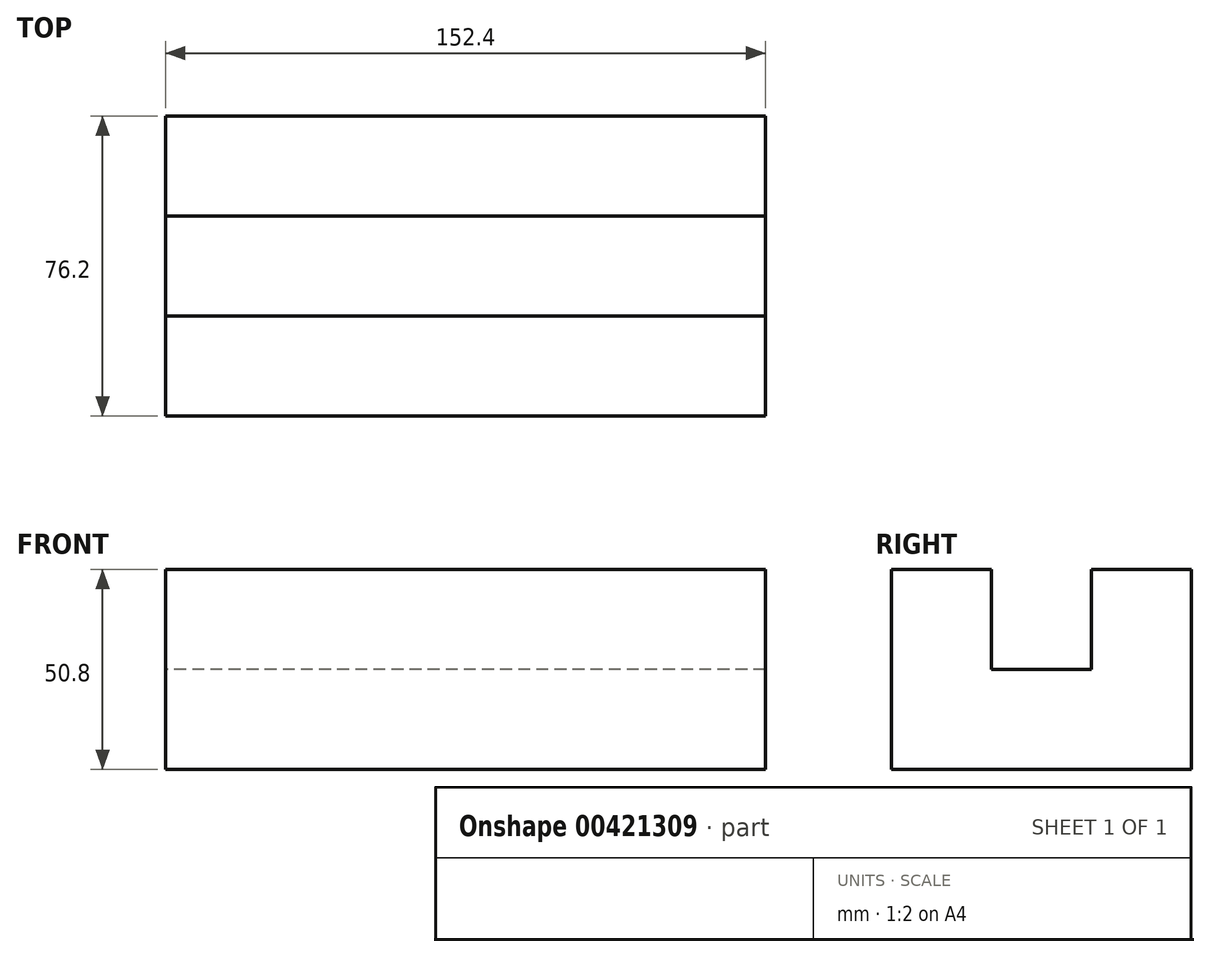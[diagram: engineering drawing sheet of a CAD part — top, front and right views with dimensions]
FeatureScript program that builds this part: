
annotation { "Feature Type Name" : "Feature", "Feature Type Description" : "" }
export const myFeature = defineFeature(function(context is Context, id is Id, definition is map)
    precondition{}
    {
        {
            var Q0;
            Q0=qCreatedBy(makeId("Right.planeOp"),FACE);
            var sketch = newSketch(context, id + "F0", { "sketchPlane" : qUnion([Q0])});
            skLineSegment(sketch, "E0", {"start": v(0, 0) * mm, "end": v(76.2, 0) * mm});
            skLineSegment(sketch, "E1", {"start": v(0, 0) * mm, "end": v(0, 50.8) * mm});
            skLineSegment(sketch, "E2", {"start": v(76.2, 0) * mm, "end": v(76.2, 50.8) * mm});
            skLineSegment(sketch, "E3", {"start": v(0, 50.8) * mm, "end": v(25.4, 50.8) * mm});
            skLineSegment(sketch, "E4", {"start": v(25.4, 50.8) * mm, "end": v(25.4, 25.4) * mm});
            skLineSegment(sketch, "E5", {"start": v(25.4, 25.4) * mm, "end": v(50.8, 25.4) * mm});
            skLineSegment(sketch, "E6", {"start": v(50.8, 25.4) * mm, "end": v(50.8, 50.8) * mm});
            skLineSegment(sketch, "E7", {"start": v(50.8, 50.8) * mm, "end": v(76.2, 50.8) * mm});
            skSolve(sketch);
        }
        {
            var Q0;
            Q0=makeQuery(id+"F0.imprint","IMPRINT",FACE,{"disambiguationData":[TD([[makeQuery(id+"F0.imprint","IMPRINT",EDGE,{"derivedFrom":sQuery(id+"F0.wireOp",EDGE,"E0")}),1.0]])]});
            extrude(context, id + "F1", {"entities" : qUnion([Q0]), "depth" : 152.4 * mm});
        }
    });
